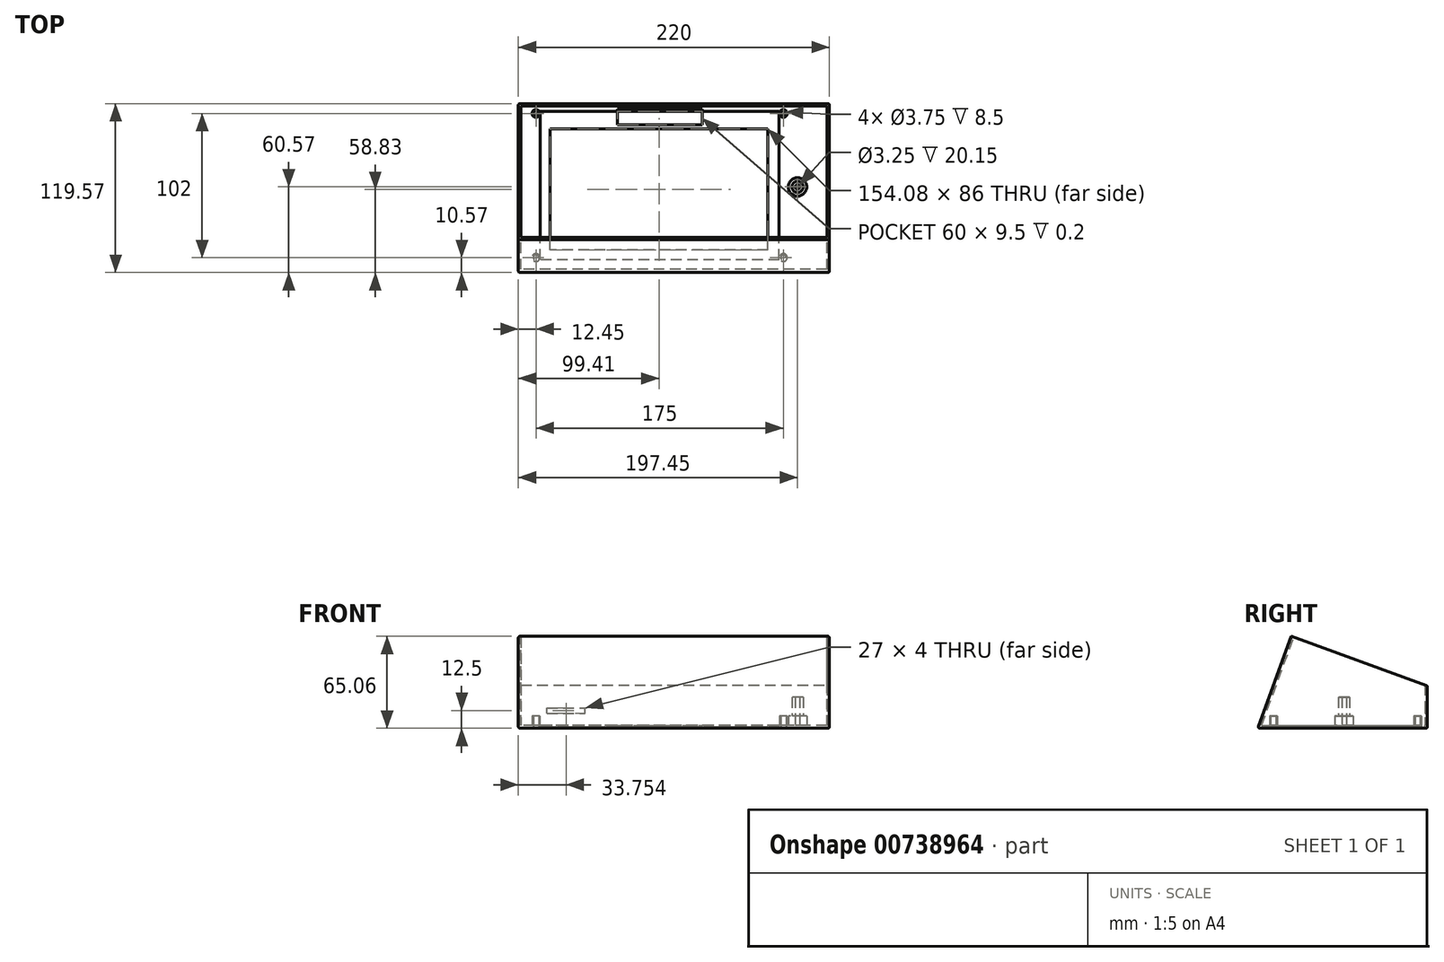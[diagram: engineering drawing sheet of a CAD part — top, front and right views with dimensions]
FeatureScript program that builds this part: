
annotation { "Feature Type Name" : "Feature", "Feature Type Description" : "" }
export const myFeature = defineFeature(function(context is Context, id is Id, definition is map)
    precondition{}
    {
        {
            var Q0;
            Q0=qCreatedBy(makeId("Top.planeOp"),FACE);
            var sketch = newSketch(context, id + "F0", { "sketchPlane" : qUnion([Q0])});
            skLineSegment(sketch, "E0.bottom", {"start": v(100.05, -62) * mm, "end": v(-99.95, -62) * mm});
            skLineSegment(sketch, "E0.top", {"start": v(99.3, 58) * mm, "end": v(-99.95, 58) * mm});
            skLineSegment(sketch, "E0.right", {"start": v(-99.95, -62) * mm, "end": v(-99.95, 58) * mm});
            skPoint(sketch, "E0.middle", {"position": v(0, 0) * mm});
            skLineSegment(sketch, "E1.bottom", {"start": v(87.5, -51) * mm, "end": v(-87.5, -51) * mm, "construction": true});
            skLineSegment(sketch, "E1.top", {"start": v(87.5, 51) * mm, "end": v(-87.5, 51) * mm, "construction": true});
            skLineSegment(sketch, "E1.left", {"start": v(87.5, -51) * mm, "end": v(87.5, 51) * mm, "construction": true});
            skLineSegment(sketch, "E1.right", {"start": v(-87.5, -51) * mm, "end": v(-87.5, 51) * mm, "construction": true});
            skLineSegment(sketch, "E2.bottom", {"start": v(84.5, -52.5) * mm, "end": v(-84.5, -52.5) * mm});
            skLineSegment(sketch, "E2.top", {"start": v(84.5, 52.5) * mm, "end": v(-84.5, 52.5) * mm});
            skLineSegment(sketch, "E2.left", {"start": v(84.5, -52.5) * mm, "end": v(84.5, 52.5) * mm});
            skLineSegment(sketch, "E2.right", {"start": v(-84.5, -52.5) * mm, "end": v(-84.5, 52.5) * mm});
            skCircle(sketch, "E3", {"center": v(-87.5, 51) * mm, "radius": 1.88 * mm});
            skCircle(sketch, "E4", {"center": v(87.5, 51) * mm, "radius": 1.88 * mm});
            skCircle(sketch, "E5", {"center": v(87.5, -51) * mm, "radius": 1.88 * mm});
            skCircle(sketch, "E6", {"center": v(-87.5, -51) * mm, "radius": 1.88 * mm});
            skLineSegment(sketch, "E7.bottom", {"start": v(76.5, -45.74) * mm, "end": v(-77.58, -45.74) * mm});
            skLineSegment(sketch, "E7.top", {"start": v(76.5, 40.26) * mm, "end": v(-77.58, 40.26) * mm});
            skLineSegment(sketch, "E7.left", {"start": v(76.5, -45.74) * mm, "end": v(76.5, 40.26) * mm});
            skLineSegment(sketch, "E7.right", {"start": v(-77.58, -45.74) * mm, "end": v(-77.58, 40.26) * mm});
            skCircle(sketch, "E8", {"center": v(-87.5, 51) * mm, "radius": 2.75 * mm});
            skCircle(sketch, "E9", {"center": v(-87.5, -51) * mm, "radius": 2.75 * mm});
            skCircle(sketch, "E10", {"center": v(87.5, -51) * mm, "radius": 2.75 * mm});
            skCircle(sketch, "E11", {"center": v(87.5, 51) * mm, "radius": 2.75 * mm});
            skPoint(sketch, "E12", {"position": v(0, 43) * mm});
            skLineSegment(sketch, "E13.bottom", {"start": v(30, 51) * mm, "end": v(-30, 51) * mm});
            skLineSegment(sketch, "E13.top", {"start": v(30, 43) * mm, "end": v(-30, 43) * mm});
            skLineSegment(sketch, "E13.left", {"start": v(30, 51) * mm, "end": v(30, 43) * mm});
            skLineSegment(sketch, "E13.right", {"start": v(-30, 51) * mm, "end": v(-30, 43) * mm});
            skLineSegment(sketch, "E14.bottom", {"start": v(100.05, -62) * mm, "end": v(120.05, -62) * mm});
            skLineSegment(sketch, "E14.top", {"start": v(99.3, 58) * mm, "end": v(120.05, 58) * mm});
            skLineSegment(sketch, "E14.right", {"start": v(120.05, -62) * mm, "end": v(120.05, 58) * mm});
            skPoint(sketch, "E15.centerSnap0", {"position": v(87.5, 0) * mm});
            skLineSegment(sketch, "E16.trimOffspring", {"start": v(99.3, 58) * mm, "end": v(99.3, 58) * mm});
            skPoint(sketch, "E17", {"position": v(100.05, 0) * mm});
            skPoint(sketch, "E18.orphan", {"position": v(100.05, 1.02) * mm});
            skPoint(sketch, "E0.left.start.orphan", {"position": v(100.05, -1.02) * mm});
            skCircle(sketch, "E19", {"center": v(97.5, -1) * mm, "radius": 1.63 * mm});
            skCircle(sketch, "E20", {"center": v(97.5, -1) * mm, "radius": 4 * mm});
            skPoint(sketch, "E15.center.orphan", {"position": v(97.5, 0) * mm});
            skCircle(sketch, "E21", {"center": v(97.5, -1) * mm, "radius": 6.5 * mm});
            skSolve(sketch);
        }
        {
            var Q0;
            Q0=makeQuery(id+"F0.imprint","IMPRINT",FACE,{"disambiguationData":[TD([[makeQuery(id+"F0.imprint","IMPRINT",EDGE,{"derivedFrom":sQuery(id+"F0.wireOp",EDGE,"E0.bottom")}),-1.0]])]});
            var Q1;
            Q1=makeQuery(id+"F0.imprint","IMPRINT",FACE,{"disambiguationData":[TD([[makeQuery(id+"F0.imprint","IMPRINT",EDGE,{"derivedFrom":sQuery(id+"F0.wireOp",EDGE,"E2.bottom")}),-1.0]])]});
            var Q2;
            Q2=makeQuery(id+"F0.imprint","IMPRINT",FACE,{"disambiguationData":[TD([[makeQuery(id+"F0.imprint","IMPRINT",EDGE,{"derivedFrom":sQuery(id+"F0.wireOp",EDGE,"E3")}),-1.0]])]});
            var Q3;
            Q3=makeQuery(id+"F0.imprint","IMPRINT",FACE,{"disambiguationData":[TD([[makeQuery(id+"F0.imprint","IMPRINT",EDGE,{"derivedFrom":sQuery(id+"F0.wireOp",EDGE,"E6")}),-1.0]])]});
            var Q4;
            Q4=makeQuery(id+"F0.imprint","IMPRINT",FACE,{"disambiguationData":[TD([[makeQuery(id+"F0.imprint","IMPRINT",EDGE,{"derivedFrom":sQuery(id+"F0.wireOp",EDGE,"E5")}),-1.0]])]});
            var Q5;
            Q5=makeQuery(id+"F0.imprint","IMPRINT",FACE,{"disambiguationData":[TD([[makeQuery(id+"F0.imprint","IMPRINT",EDGE,{"derivedFrom":sQuery(id+"F0.wireOp",EDGE,"E4")}),-1.0]])]});
            var Q6;
            {var subQ5=sQuery(id+"F0.wireOp",EDGE,"E13.top");Q6=makeQuery(id+"F0.imprint","IMPRINT",FACE,{"disambiguationData":[TD([[makeQuery(id+"F0.imprint","IMPRINT",EDGE,{"derivedFrom":subQ5}),-1.0]])]});}
            var Q7;
            {var subQ5=sQuery(id+"F0.wireOp",EDGE,"E13.bottom");Q7=makeQuery(id+"F0.imprint","IMPRINT",FACE,{"disambiguationData":[TD([[makeQuery(id+"F0.imprint","IMPRINT",EDGE,{"derivedFrom":subQ5}),1.0]])]});}
            var Q8;
            Q8=makeQuery(id+"F0.imprint","IMPRINT",FACE,{"disambiguationData":[TD([[makeQuery(id+"F0.imprint","IMPRINT",EDGE,{"derivedFrom":sQuery(id+"F0.wireOp",EDGE,"E7.bottom")}),-1.0]])]});
            var Q9;
            Q9=makeQuery(id+"F0.imprint","IMPRINT",FACE,{"disambiguationData":[TD([[makeQuery(id+"F0.imprint","IMPRINT",EDGE,{"derivedFrom":sQuery(id+"F0.wireOp",EDGE,"E15")}),-1.0]])]});
            var Q10;
            Q10=makeQuery(id+"F0.imprint","IMPRINT",FACE,{"disambiguationData":[TD([[makeQuery(id+"F0.imprint","IMPRINT",EDGE,{"derivedFrom":sQuery(id+"F0.wireOp",EDGE,"E6")}),1.0]])]});
            var Q11;
            Q11=makeQuery(id+"F0.imprint","IMPRINT",FACE,{"disambiguationData":[TD([[makeQuery(id+"F0.imprint","IMPRINT",EDGE,{"derivedFrom":sQuery(id+"F0.wireOp",EDGE,"E3")}),1.0]])]});
            var Q12;
            Q12=makeQuery(id+"F0.imprint","IMPRINT",FACE,{"disambiguationData":[TD([[makeQuery(id+"F0.imprint","IMPRINT",EDGE,{"derivedFrom":sQuery(id+"F0.wireOp",EDGE,"E15")}),1.0]])]});
            var Q13;
            Q13=makeQuery(id+"F0.imprint","IMPRINT",FACE,{"disambiguationData":[TD([[makeQuery(id+"F0.imprint","IMPRINT",EDGE,{"derivedFrom":sQuery(id+"F0.wireOp",EDGE,"E5")}),1.0]])]});
            var Q14;
            Q14=makeQuery(id+"F0.imprint","IMPRINT",FACE,{"disambiguationData":[TD([[makeQuery(id+"F0.imprint","IMPRINT",EDGE,{"derivedFrom":sQuery(id+"F0.wireOp",EDGE,"E4")}),1.0]])]});
            extrude(context, id + "F1", {"entities" : qUnion([Q0, Q1, Q2, Q3, Q4, Q5, Q6, Q7, Q8, Q9, Q10, Q11, Q12, Q13, Q14]), "depth" : 30 * mm, "offsetDistance" : 25 * mm});
        }
        {
            var Q0;
            Q0=makeQuery(id+"F1.opExtrude","SWEPT_FACE",FACE,{"disambiguationData":[OSD([sQuery(id+"F0.wireOp",EDGE,"E0.right")])]});
            var sketch = newSketch(context, id + "F2", { "sketchPlane" : qUnion([Q0])});
            skLineSegment(sketch, "E22.0", {"start": v(62, 0) * mm, "end": v(-58, 0) * mm});
            skLineSegment(sketch, "E22.1", {"start": v(-58, 30) * mm, "end": v(-58, 0) * mm});
            skLineSegment(sketch, "E22.2", {"start": v(62, 30) * mm, "end": v(-58, 30) * mm});
            skLineSegment(sketch, "E22.3", {"start": v(62, 30) * mm, "end": v(62, 0) * mm});
            skLineSegment(sketch, "E23", {"start": v(62, 0) * mm, "end": v(38.32, 65.06) * mm});
            skLineSegment(sketch, "E24", {"start": v(38.32, 65.06) * mm, "end": v(-58, 30) * mm});
            skSolve(sketch);
        }
        {
            var Q0;
            {var subQ0=sQuery(id+"F2.wireOp",EDGE,"E22.3");Q0=makeQuery(id+"F2.imprint","IMPRINT",FACE,{"disambiguationData":[TD([[makeQuery(id+"F2.imprint","IMPRINT",EDGE,{"derivedFrom":subQ0}),-1.0]])]});}
            extrude(context, id + "F3", {"entities" : qUnion([Q0]), "operationType" : NewBodyOperationType.REMOVE, "endBound" : BoundingType.THROUGH_ALL, "oppositeDirection" : true, "depth" : 25 * mm, "offsetDistance" : 25 * mm});
        }
        {
            var Q0;
            {var subQ0=sQuery(id+"F2.wireOp",EDGE,"E24");Q0=makeQuery(id+"F2.imprint","IMPRINT",FACE,{"disambiguationData":[TD([[makeQuery(id+"F2.imprint","IMPRINT",EDGE,{"derivedFrom":subQ0}),1.0]])]});}
            var Q1;
            {var subQ0=sQuery(id+"F2.wireOp",EDGE,"E22.0");Q1=makeQuery(id+"F2.imprint","IMPRINT",FACE,{"disambiguationData":[TD([[makeQuery(id+"F2.imprint","IMPRINT",EDGE,{"derivedFrom":subQ0}),-1.0]])]});}
            var Q2;
            Q2=makeQuery(id+"F1.opExtrude","SWEPT_FACE",FACE,{"disambiguationData":[OSD([sQuery(id+"F0.wireOp",EDGE,"E14.right")])]});
            extrude(context, id + "F4", {"entities" : qUnion([Q0, Q1]), "operationType" : NewBodyOperationType.ADD, "endBound" : BoundingType.UP_TO_SURFACE, "oppositeDirection" : true, "depth" : 25 * mm, "endBoundEntityFace" : qUnion([Q2]), "offsetDistance" : 25 * mm});
        }
        {
            var Q0;
            Q0=makeQuery(id+"F4.opExtrude","SWEPT_FACE",FACE,{"disambiguationData":[OSD([sQuery(id+"F2.wireOp",EDGE,"E24")])]});
            shell(context, id + "F5", {"entities" : qUnion([Q0]), "thickness" : 1.85 * mm});
        }
        {
            var Q0;
            Q0=makeQuery(id+"F0.imprint","IMPRINT",FACE,{"disambiguationData":[TD([[makeQuery(id+"F0.imprint","IMPRINT",EDGE,{"derivedFrom":sQuery(id+"F0.wireOp",EDGE,"E5")}),-1.0]])]});
            var Q1;
            Q1=makeQuery(id+"F0.imprint","IMPRINT",FACE,{"disambiguationData":[TD([[makeQuery(id+"F0.imprint","IMPRINT",EDGE,{"derivedFrom":sQuery(id+"F0.wireOp",EDGE,"E4")}),-1.0]])]});
            var Q2;
            Q2=makeQuery(id+"F0.imprint","IMPRINT",FACE,{"disambiguationData":[TD([[makeQuery(id+"F0.imprint","IMPRINT",EDGE,{"derivedFrom":sQuery(id+"F0.wireOp",EDGE,"E6")}),-1.0]])]});
            var Q3;
            Q3=makeQuery(id+"F0.imprint","IMPRINT",FACE,{"disambiguationData":[TD([[makeQuery(id+"F0.imprint","IMPRINT",EDGE,{"derivedFrom":sQuery(id+"F0.wireOp",EDGE,"E3")}),-1.0]])]});
            var Q4;
            Q4=makeQuery(id+"F0.imprint","IMPRINT",FACE,{"disambiguationData":[TD([[makeQuery(id+"F0.imprint","IMPRINT",EDGE,{"derivedFrom":sQuery(id+"F0.wireOp",EDGE,"E20")}),-1.0]])]});
            extrude(context, id + "F6", {"entities" : qUnion([Q0, Q1, Q2, Q3, Q4]), "operationType" : NewBodyOperationType.ADD, "depth" : 8.5 * mm, "offsetDistance" : 25 * mm});
        }
        {
            var Q0;
            Q0=makeQuery(id+"F0.imprint","IMPRINT",FACE,{"disambiguationData":[TD([[makeQuery(id+"F0.imprint","IMPRINT",EDGE,{"derivedFrom":sQuery(id+"F0.wireOp",EDGE,"E19")}),-1.0]])]});
            extrude(context, id + "F7", {"entities" : qUnion([Q0]), "operationType" : NewBodyOperationType.ADD, "depth" : 22 * mm, "offsetDistance" : 25 * mm});
        }
        {
            var Q0;
            Q0=makeQuery(id+"F0.imprint","IMPRINT",FACE,{"disambiguationData":[TD([[makeQuery(id+"F0.imprint","IMPRINT",EDGE,{"derivedFrom":sQuery(id+"F0.wireOp",EDGE,"E5")}),1.0]])]});
            var Q1;
            Q1=makeQuery(id+"F0.imprint","IMPRINT",FACE,{"disambiguationData":[TD([[makeQuery(id+"F0.imprint","IMPRINT",EDGE,{"derivedFrom":sQuery(id+"F0.wireOp",EDGE,"E6")}),1.0]])]});
            var Q2;
            Q2=makeQuery(id+"F0.imprint","IMPRINT",FACE,{"disambiguationData":[TD([[makeQuery(id+"F0.imprint","IMPRINT",EDGE,{"derivedFrom":sQuery(id+"F0.wireOp",EDGE,"E3")}),1.0]])]});
            var Q3;
            Q3=makeQuery(id+"F0.imprint","IMPRINT",FACE,{"disambiguationData":[TD([[makeQuery(id+"F0.imprint","IMPRINT",EDGE,{"derivedFrom":sQuery(id+"F0.wireOp",EDGE,"E4")}),1.0]])]});
            var Q4;
            {var subQ1=sQuery(id+"F0.wireOp",EDGE,"E0.right");var subQ2=sQuery(id+"F0.wireOp",EDGE,"E0.left");var subQ3=sQuery(id+"F0.wireOp",EDGE,"E0.top");Q4=makeQuery(id+"F6.boolean.opBoolean","SPLIT",FACE,{"disambiguationData":[TD([makeQuery(id+"FxlOXKSclYgFQFW_1.opShell","OFFSET_FACE",FACE,{"disambiguationData":[OSD([subQ3])]})])],"derivedFrom":makeQuery(id+"FxlOXKSclYgFQFW_1.opShell","OFFSET_FACE",FACE,{"disambiguationData":[OSD([sQuery(id+"F0.wireOp",EDGE,"E0.bottom"),subQ3,subQ2,subQ1])]})});}
            extrude(context, id + "F8", {"entities" : qUnion([Q0, Q1, Q2, Q3]), "operationType" : NewBodyOperationType.REMOVE, "endBound" : BoundingType.UP_TO_NEXT, "depth" : 25 * mm, "endBoundEntityFace" : qUnion([Q4]), "offsetDistance" : 25 * mm});
        }
        {
            var Q0;
            Q0=makeQuery(id+"F0.imprint","IMPRINT",FACE,{"disambiguationData":[TD([[makeQuery(id+"F0.imprint","IMPRINT",EDGE,{"derivedFrom":sQuery(id+"F0.wireOp",EDGE,"E7.bottom")}),-1.0]])]});
            extrude(context, id + "F9", {"entities" : qUnion([Q0]), "operationType" : NewBodyOperationType.REMOVE, "endBound" : BoundingType.UP_TO_NEXT, "depth" : 25 * mm, "offsetDistance" : 25 * mm});
        }
        {
            var Q0;
            {var subQ0=sQuery(id+"F0.wireOp",EDGE,"E14.right");var subQ2=sQuery(id+"F2.wireOp",EDGE,"E23");var subQ3=sQuery(id+"F0.wireOp",EDGE,"E0.right");var subQ5=makeQuery(id+"F5.opShell","OFFSET_FACE",FACE,{"disambiguationData":[OSD([subQ2])]});var subQ6=sQuery(id+"F0.wireOp",EDGE,"E14.top");var subQ7=sQuery(id+"F0.wireOp",EDGE,"E0.top");Q0=makeQuery(id+"F7.boolean.opBoolean","SPLIT",FACE,{"disambiguationData":[TD([subQ5])],"derivedFrom":makeQuery(id+"F6.boolean.opBoolean","SPLIT",FACE,{"disambiguationData":[TD([subQ5])],"derivedFrom":makeQuery(id+"F5.opShell","OFFSET_FACE",FACE,{"disambiguationData":[OSD([sQuery(id+"F0.wireOp",EDGE,"E0.bottom"),subQ7,subQ3,sQuery(id+"F0.wireOp",EDGE,"E14.bottom"),subQ6,subQ0])]})})});}
            var sketch = newSketch(context, id + "F10", { "sketchPlane" : qUnion([Q0])});
            skLineSegment(sketch, "E25.0", {"start": v(84.5, 52.5) * mm, "end": v(-84.5, 52.5) * mm});
            skLineSegment(sketch, "E25.1", {"start": v(-30, 52.5) * mm, "end": v(-30, 43) * mm});
            skLineSegment(sketch, "E25.2", {"start": v(30, 43) * mm, "end": v(-30, 43) * mm});
            skLineSegment(sketch, "E25.3", {"start": v(30, 52.5) * mm, "end": v(30, 43) * mm});
            skLineSegment(sketch, "E25.4", {"start": v(84.5, -52.5) * mm, "end": v(84.5, 52.5) * mm});
            skLineSegment(sketch, "E25.5", {"start": v(-84.5, -52.5) * mm, "end": v(-84.5, 52.5) * mm});
            skLineSegment(sketch, "E25.6", {"start": v(84.5, -52.5) * mm, "end": v(-84.5, -52.5) * mm});
            skLineSegment(sketch, "E26.bottom", {"start": v(-30, 52.5) * mm, "end": v(30, 52.5) * mm});
            skLineSegment(sketch, "E26.top", {"start": v(-30, 54) * mm, "end": v(30, 54) * mm});
            skLineSegment(sketch, "E26.left", {"start": v(-30, 52.5) * mm, "end": v(-30, 54) * mm});
            skLineSegment(sketch, "E26.right", {"start": v(30, 52.5) * mm, "end": v(30, 54) * mm});
            skSolve(sketch);
        }
        {
            var Q0;
            Q0 = qSketchRegion(id + "F10", true);
            extrude(context, id + "F11", {"entities" : qUnion([Q0]), "operationType" : NewBodyOperationType.REMOVE, "oppositeDirection" : true, "depth" : 1 * mm, "offsetDistance" : 25 * mm});
        }
        {
            var Q0;
            {var subQ0=sQuery(id+"F10.wireOp",EDGE,"E25.1");Q0=makeQuery(id+"F10.imprint","IMPRINT",FACE,{"disambiguationData":[TD([[makeQuery(id+"F10.imprint","IMPRINT",EDGE,{"derivedFrom":subQ0}),1.0]])]});}
            var Q1;
            Q1=makeQuery(id+"F10.imprint","IMPRINT",FACE,{"disambiguationData":[TD([[makeQuery(id+"F10.imprint","IMPRINT",EDGE,{"derivedFrom":sQuery(id+"F10.wireOp",EDGE,"E26.bottom")}),1.0]])]});
            extrude(context, id + "F12", {"entities" : qUnion([Q0, Q1]), "operationType" : NewBodyOperationType.REMOVE, "oppositeDirection" : true, "depth" : 1.2 * mm, "offsetDistance" : 25 * mm});
        }
        {
            var Q0;
            Q0=makeQuery(id+"F1.opExtrude","SWEPT_FACE",FACE,{"disambiguationData":[OSD([sQuery(id+"F0.wireOp",EDGE,"E0.top"),sQuery(id+"F0.wireOp",EDGE,"E14.top")])]});
            var sketch = newSketch(context, id + "F13", { "sketchPlane" : qUnion([Q0])});
            skLineSegment(sketch, "E27.bottom", {"start": v(79.7, 10.5) * mm, "end": v(52.7, 10.5) * mm});
            skLineSegment(sketch, "E27.top", {"start": v(79.7, 14.5) * mm, "end": v(52.7, 14.5) * mm});
            skLineSegment(sketch, "E27.left", {"start": v(79.7, 10.5) * mm, "end": v(79.7, 14.5) * mm});
            skLineSegment(sketch, "E27.right", {"start": v(52.7, 10.5) * mm, "end": v(52.7, 14.5) * mm});
            skLineSegment(sketch, "E28.0", {"start": v(-99, 0) * mm, "end": v(99, 0) * mm});
            skLineSegment(sketch, "E29.0", {"start": v(99.95, 30) * mm, "end": v(99.95, 0) * mm});
            skSolve(sketch);
        }
        {
            var Q0;
            Q0=makeQuery(id+"F13.imprint","IMPRINT",FACE,{"disambiguationData":[TD([[makeQuery(id+"F13.imprint","IMPRINT",EDGE,{"derivedFrom":sQuery(id+"F13.wireOp",EDGE,"E27.bottom")}),-1.0]])]});
            var Q1;
            Q1=makeQuery(id+"FxlOXKSclYgFQFW_1.opShell","OFFSET_FACE",FACE,{"disambiguationData":[OSD([sQuery(id+"F0.wireOp",EDGE,"E0.top")])]});
            extrude(context, id + "F14", {"entities" : qUnion([Q0]), "operationType" : NewBodyOperationType.REMOVE, "endBound" : BoundingType.UP_TO_NEXT, "oppositeDirection" : true, "depth" : 25 * mm, "endBoundEntityFace" : qUnion([Q1]), "offsetDistance" : 25 * mm});
        }
        {
            var Q0;
            Q0=makeQuery(id+"F1.opExtrude","CAP_EDGE",EDGE,{"disambiguationData":[OSD([sQuery(id+"F0.wireOp",EDGE,"E0.right")])],"isStart":true});
            var Q1;
            Q1=makeQuery(id+"F1.opExtrude","CAP_EDGE",EDGE,{"disambiguationData":[OSD([sQuery(id+"F0.wireOp",EDGE,"E14.right")])],"isStart":true});
            var Q2;
            Q2=makeQuery(id+"F1.opExtrude","CAP_EDGE",EDGE,{"disambiguationData":[OSD([sQuery(id+"F0.wireOp",EDGE,"E0.top"),sQuery(id+"F0.wireOp",EDGE,"E14.top")])],"isStart":true});
            var Q3;
            Q3=makeQuery(id+"F1.opExtrude","SWEPT_EDGE",EDGE,{"disambiguationData":[OSD([sQuery(id+"F0.wireOp",EDGE,"E14.top"),sQuery(id+"F0.wireOp",EDGE,"E14.right")])]});
            var Q4;
            Q4=makeQuery(id+"F1.opExtrude","SWEPT_EDGE",EDGE,{"disambiguationData":[OSD([sQuery(id+"F0.wireOp",EDGE,"E0.top"),sQuery(id+"F0.wireOp",EDGE,"E0.right")])]});
            var Q5;
            Q5=makeQuery(id+"F4.boolean.opBoolean","MERGE",EDGE,{"derivedFrom":[makeQuery(id+"F1.opExtrude","CAP_EDGE",EDGE,{"disambiguationData":[OSD([sQuery(id+"F0.wireOp",EDGE,"E0.top"),sQuery(id+"F0.wireOp",EDGE,"E14.top")])],"isStart":false}),makeQuery(id+"F4.opExtrude","SWEPT_EDGE",EDGE,{"disambiguationData":[OSD([sQuery(id+"F2.wireOp",EDGE,"E22.1"),sQuery(id+"F2.wireOp",EDGE,"E22.2"),sQuery(id+"F2.wireOp",EDGE,"E24")])]})]});
            var Q6;
            {var subQ0=sQuery(id+"F2.wireOp",EDGE,"E23");Q6=makeQuery(id+"F4.boolean.opBoolean","MERGE",EDGE,{"derivedFrom":[makeQuery(id+"F3.boolean.opBoolean","COPY",EDGE,{"derivedFrom":makeQuery(id+"F3.opExtrude","CAP_EDGE",EDGE,{"disambiguationData":[OSD([subQ0])],"isStart":true})}),makeQuery(id+"F4.opExtrude","CAP_EDGE",EDGE,{"disambiguationData":[OSD([subQ0])],"isStart":true})]});}
            var Q7;
            Q7=makeQuery(id+"F4.opExtrude","CAP_EDGE",EDGE,{"disambiguationData":[OSD([sQuery(id+"F2.wireOp",EDGE,"E24")])],"isStart":true});
            var Q8;
            Q8=makeQuery(id+"F4.opExtrude","CAP_EDGE",EDGE,{"disambiguationData":[OSD([sQuery(id+"F2.wireOp",EDGE,"E24")])],"isStart":false});
            var Q9;
            {var subQ0=sQuery(id+"F2.wireOp",EDGE,"E23");Q9=makeQuery(id+"F4.boolean.opBoolean","MERGE",EDGE,{"derivedFrom":[makeQuery(id+"F3.boolean.opBoolean","INTERSECT",EDGE,{"derivedFrom":[makeQuery(id+"F1.opExtrude","SWEPT_FACE",FACE,{"disambiguationData":[OSD([sQuery(id+"F0.wireOp",EDGE,"E14.right")])]}),makeQuery(id+"F3.opExtrude","SWEPT_FACE",FACE,{"disambiguationData":[OSD([subQ0])]})]}),makeQuery(id+"F4.opExtrude","CAP_EDGE",EDGE,{"disambiguationData":[OSD([subQ0])],"isStart":false})]});}
            var Q10;
            Q10=makeQuery(id+"F3.boolean.opBoolean","MERGE",EDGE,{"derivedFrom":[makeQuery(id+"F1.opExtrude","CAP_EDGE",EDGE,{"disambiguationData":[OSD([sQuery(id+"F0.wireOp",EDGE,"E0.bottom"),sQuery(id+"F0.wireOp",EDGE,"E14.bottom")])],"isStart":true}),makeQuery(id+"F3.opExtrude","SWEPT_EDGE",EDGE,{"disambiguationData":[OSD([sQuery(id+"F2.wireOp",EDGE,"E22.0"),sQuery(id+"F2.wireOp",EDGE,"E22.3"),sQuery(id+"F2.wireOp",EDGE,"E23")])]})]});
            var Q11;
            Q11=makeQuery(id+"F14.boolean.opBoolean","COPY",EDGE,{"derivedFrom":makeQuery(id+"F14.opExtrude","CAP_EDGE",EDGE,{"disambiguationData":[OSD([sQuery(id+"F13.wireOp",EDGE,"E27.top")])],"isStart":true})});
            var Q12;
            Q12=makeQuery(id+"F14.boolean.opBoolean","COPY",EDGE,{"derivedFrom":makeQuery(id+"F14.opExtrude","CAP_EDGE",EDGE,{"disambiguationData":[OSD([sQuery(id+"F13.wireOp",EDGE,"E27.left")])],"isStart":true})});
            var Q13;
            Q13=makeQuery(id+"F14.boolean.opBoolean","COPY",EDGE,{"derivedFrom":makeQuery(id+"F14.opExtrude","CAP_EDGE",EDGE,{"disambiguationData":[OSD([sQuery(id+"F13.wireOp",EDGE,"E27.bottom")])],"isStart":true})});
            var Q14;
            Q14=makeQuery(id+"F14.boolean.opBoolean","COPY",EDGE,{"derivedFrom":makeQuery(id+"F14.opExtrude","CAP_EDGE",EDGE,{"disambiguationData":[OSD([sQuery(id+"F13.wireOp",EDGE,"E27.right")])],"isStart":true})});
            var Q15;
            Q15=makeQuery(id+"F14.boolean.opBoolean","COPY",EDGE,{"derivedFrom":makeQuery(id+"F14.opExtrude","CAP_EDGE",EDGE,{"disambiguationData":[OSD([sQuery(id+"F13.wireOp",EDGE,"E27.top")])],"isStart":false})});
            var Q16;
            Q16=makeQuery(id+"F14.boolean.opBoolean","COPY",EDGE,{"derivedFrom":makeQuery(id+"F14.opExtrude","CAP_EDGE",EDGE,{"disambiguationData":[OSD([sQuery(id+"F13.wireOp",EDGE,"E27.left")])],"isStart":false})});
            var Q17;
            Q17=makeQuery(id+"F14.boolean.opBoolean","COPY",EDGE,{"derivedFrom":makeQuery(id+"F14.opExtrude","CAP_EDGE",EDGE,{"disambiguationData":[OSD([sQuery(id+"F13.wireOp",EDGE,"E27.bottom")])],"isStart":false})});
            var Q18;
            Q18=makeQuery(id+"F14.boolean.opBoolean","COPY",EDGE,{"derivedFrom":makeQuery(id+"F14.opExtrude","CAP_EDGE",EDGE,{"disambiguationData":[OSD([sQuery(id+"F13.wireOp",EDGE,"E27.right")])],"isStart":false})});
            fillet(context, id + "F15", {"entities" : qUnion([Q0, Q1, Q2, Q3, Q4, Q5, Q6, Q7, Q8, Q9, Q10, Q11, Q12, Q13, Q14, Q15, Q16, Q17, Q18]), "radius" : 1 * mm, "tangentPropagation" : true, "allowEdgeOverflow" : false});
        }
    });
